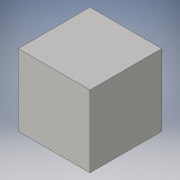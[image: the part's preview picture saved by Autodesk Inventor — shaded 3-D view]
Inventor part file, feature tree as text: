
AUTODESK INVENTOR PART (.ipt)
format: ipt  version: 2016 (Build 200138000, 138)  size: 80,384 bytes
history: native  units: in
note: dims shown in document units (in); Inventor stores cm internally (conversion verified against a paired STEP export)
features: extrude x1, sketch x1
ambient origin geometry x8: Origin, YZ Plane, XZ Plane, XY Plane, X Axis, Y Axis, Z Axis, Center Point
bodies: Solid1 (feature_tree)
feature tree (2):
  extrude  "Extrusion1"  Depth=0.75in
  sketch  "Sketch1"  dims[d0=0.75in d1=0.75in d2=0.75in d3=0.0in]
